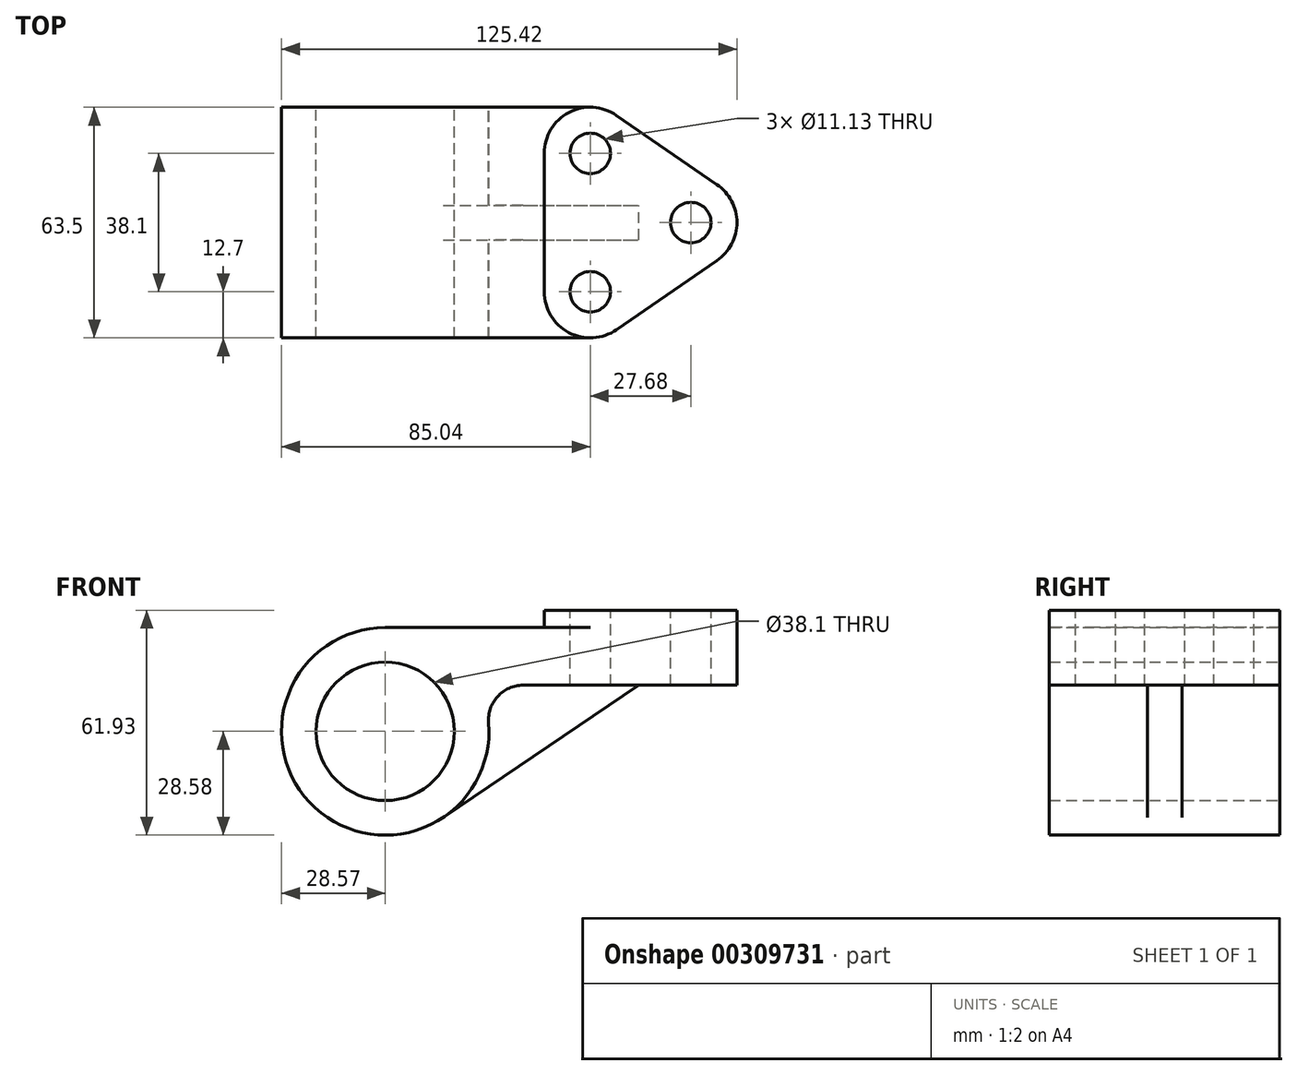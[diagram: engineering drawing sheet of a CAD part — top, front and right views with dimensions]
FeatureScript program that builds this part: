
annotation { "Feature Type Name" : "Feature", "Feature Type Description" : "" }
export const myFeature = defineFeature(function(context is Context, id is Id, definition is map)
    precondition{}
    {
        {
            var Q0;
            Q0=qCreatedBy(makeId("Front.planeOp"),FACE);
            var sketch = newSketch(context, id + "F0", { "sketchPlane" : qUnion([Q0])});
            skArc(sketch, "E0", {"start": v(0, 28.58) * mm, "mid": v(-19.35, -21.03) * mm, "end": v(28.48, 2.38) * mm});
            skCircle(sketch, "E1", {"center": v(0, 0) * mm, "radius": 19.05 * mm});
            skLineSegment(sketch, "E2", {"start": v(0, 28.58) * mm, "end": v(96.85, 28.58) * mm});
            skArc(sketch, "E3", {"start": v(37.97, 12.7) * mm, "mid": v(30.96, 9.62) * mm, "end": v(28.48, 2.38) * mm});
            skLineSegment(sketch, "E4", {"start": v(37.97, 12.7) * mm, "end": v(96.85, 12.7) * mm});
            skLineSegment(sketch, "E5", {"start": v(96.85, 12.7) * mm, "end": v(96.85, 28.58) * mm});
            skSolve(sketch);
        }
        {
            var Q0;
            Q0 = qSketchRegion(id + "F0", true);
            extrude(context, id + "F1", {"entities" : qUnion([Q0]), "depth" : 63.5 * mm});
        }
        {
            var Q0;
            Q0=makeQuery(id+"F1.opExtrude","SWEPT_FACE",FACE,{"disambiguationData":[OSD([sQuery(id+"F0.wireOp",EDGE,"E2")])]});
            var sketch = newSketch(context, id + "F2", { "sketchPlane" : qUnion([Q0])});
            skArc(sketch, "E6", {"start": v(63.67, -2.24) * mm, "mid": v(50.56, -1.46) * mm, "end": v(43.77, -12.7) * mm});
            skArc(sketch, "E7", {"start": v(43.77, -50.8) * mm, "mid": v(50.56, -62.04) * mm, "end": v(63.67, -61.26) * mm});
            skArc(sketch, "E8", {"start": v(91.35, -42.21) * mm, "mid": v(96.85, -31.75) * mm, "end": v(91.35, -21.29) * mm});
            skLineSegment(sketch, "E9", {"start": v(43.77, -12.7) * mm, "end": v(43.77, -50.8) * mm});
            skLineSegment(sketch, "E10", {"start": v(63.67, -61.26) * mm, "end": v(91.35, -42.21) * mm});
            skLineSegment(sketch, "E11", {"start": v(63.67, -2.24) * mm, "end": v(91.35, -21.29) * mm});
            skPoint(sketch, "E12", {"position": v(96.85, -31.75) * mm});
            skSolve(sketch);
        }
        {
            var Q0;
            Q0 = qSketchRegion(id + "F2", true);
            extrude(context, id + "F3", {"entities" : qUnion([Q0]), "operationType" : NewBodyOperationType.ADD, "depth" : 4.78 * mm});
        }
        {
            var Q0;
            Q0=makeQuery(id+"F3.opExtrude","CAP_FACE",FACE,{"disambiguationData":[OSD([sQuery(id+"F2.wireOp",EDGE,"E6"),sQuery(id+"F2.wireOp",EDGE,"E7"),sQuery(id+"F2.wireOp",EDGE,"E8"),sQuery(id+"F2.wireOp",EDGE,"E9"),sQuery(id+"F2.wireOp",EDGE,"E10"),sQuery(id+"F2.wireOp",EDGE,"E11")])],"isStart":false});
            var sketch = newSketch(context, id + "F4", { "sketchPlane" : qUnion([Q0])});
            skArc(sketch, "E13.0", {"start": v(63.67, -2.24) * mm, "mid": v(60.24, -0.57) * mm, "end": v(56.47, 0) * mm});
            skArc(sketch, "E14.0", {"start": v(56.47, -63.5) * mm, "mid": v(60.24, -62.93) * mm, "end": v(63.67, -61.26) * mm});
            skLineSegment(sketch, "E15.0", {"start": v(63.67, -61.26) * mm, "end": v(91.35, -42.21) * mm});
            skLineSegment(sketch, "E16.0", {"start": v(63.67, -2.24) * mm, "end": v(91.35, -21.29) * mm});
            skArc(sketch, "E17.0", {"start": v(91.35, -42.21) * mm, "mid": v(96.85, -31.75) * mm, "end": v(91.35, -21.29) * mm});
            skCircle(sketch, "E18", {"center": v(56.47, -12.7) * mm, "radius": 5.56 * mm});
            skCircle(sketch, "E19", {"center": v(56.47, -50.8) * mm, "radius": 5.56 * mm});
            skCircle(sketch, "E20", {"center": v(84.15, -31.75) * mm, "radius": 5.56 * mm});
            skLineSegment(sketch, "E21", {"start": v(56.47, -63.5) * mm, "end": v(57.47, -69.57) * mm});
            skLineSegment(sketch, "E22", {"start": v(57.47, -69.57) * mm, "end": v(104.9, -69.57) * mm});
            skLineSegment(sketch, "E23", {"start": v(104.9, -69.57) * mm, "end": v(103.15, 2.34) * mm});
            skLineSegment(sketch, "E24", {"start": v(103.15, 2.34) * mm, "end": v(60.49, 3.72) * mm});
            skLineSegment(sketch, "E25", {"start": v(60.49, 3.72) * mm, "end": v(56.47, 0) * mm});
            skPoint(sketch, "E26.orphan", {"position": v(43.77, -12.7) * mm});
            skPoint(sketch, "E27.orphan", {"position": v(43.77, -50.8) * mm});
            skSolve(sketch);
        }
        {
            var Q0;
            Q0 = qSketchRegion(id + "F4", true);
            extrude(context, id + "F5", {"entities" : qUnion([Q0]), "operationType" : NewBodyOperationType.REMOVE, "endBound" : BoundingType.THROUGH_ALL, "oppositeDirection" : true, "depth" : 25.4 * mm});
        }
        {
            var Q0;
            Q0=qCreatedBy(makeId("Front.planeOp"),FACE);
            var sketch = newSketch(context, id + "F6", { "sketchPlane" : qUnion([Q0])});
            skArc(sketch, "E28.0", {"start": v(16, -23.68) * mm, "mid": v(25.77, -12.34) * mm, "end": v(28.48, 2.38) * mm});
            skLineSegment(sketch, "E29.0", {"start": v(63.67, 12.7) * mm, "end": v(91.35, 12.7) * mm});
            skLineSegment(sketch, "E30.0", {"start": v(56.47, 12.7) * mm, "end": v(63.67, 12.7) * mm});
            skPoint(sketch, "E31.0", {"position": v(47.22, 12.7) * mm});
            skLineSegment(sketch, "E32.0", {"start": v(37.97, 12.7) * mm, "end": v(56.47, 12.7) * mm});
            skArc(sketch, "E33.0", {"start": v(37.97, 12.7) * mm, "mid": v(30.96, 9.62) * mm, "end": v(28.48, 2.38) * mm});
            skLineSegment(sketch, "E34", {"start": v(16, -23.68) * mm, "end": v(69.85, 12.7) * mm});
            skPoint(sketch, "E35.orphan", {"position": v(0, 28.58) * mm});
            skSolve(sketch);
        }
        {
            var Q0;
            Q0 = qSketchRegion(id + "F6", true);
            extrude(context, id + "F7", {"entities" : qUnion([Q0]), "operationType" : NewBodyOperationType.ADD, "depth" : 36.5 * mm, "hasSecondDirection" : true, "secondDirectionOppositeDirection" : false, "secondDirectionDepth" : 26.99 * mm});
        }
    });
